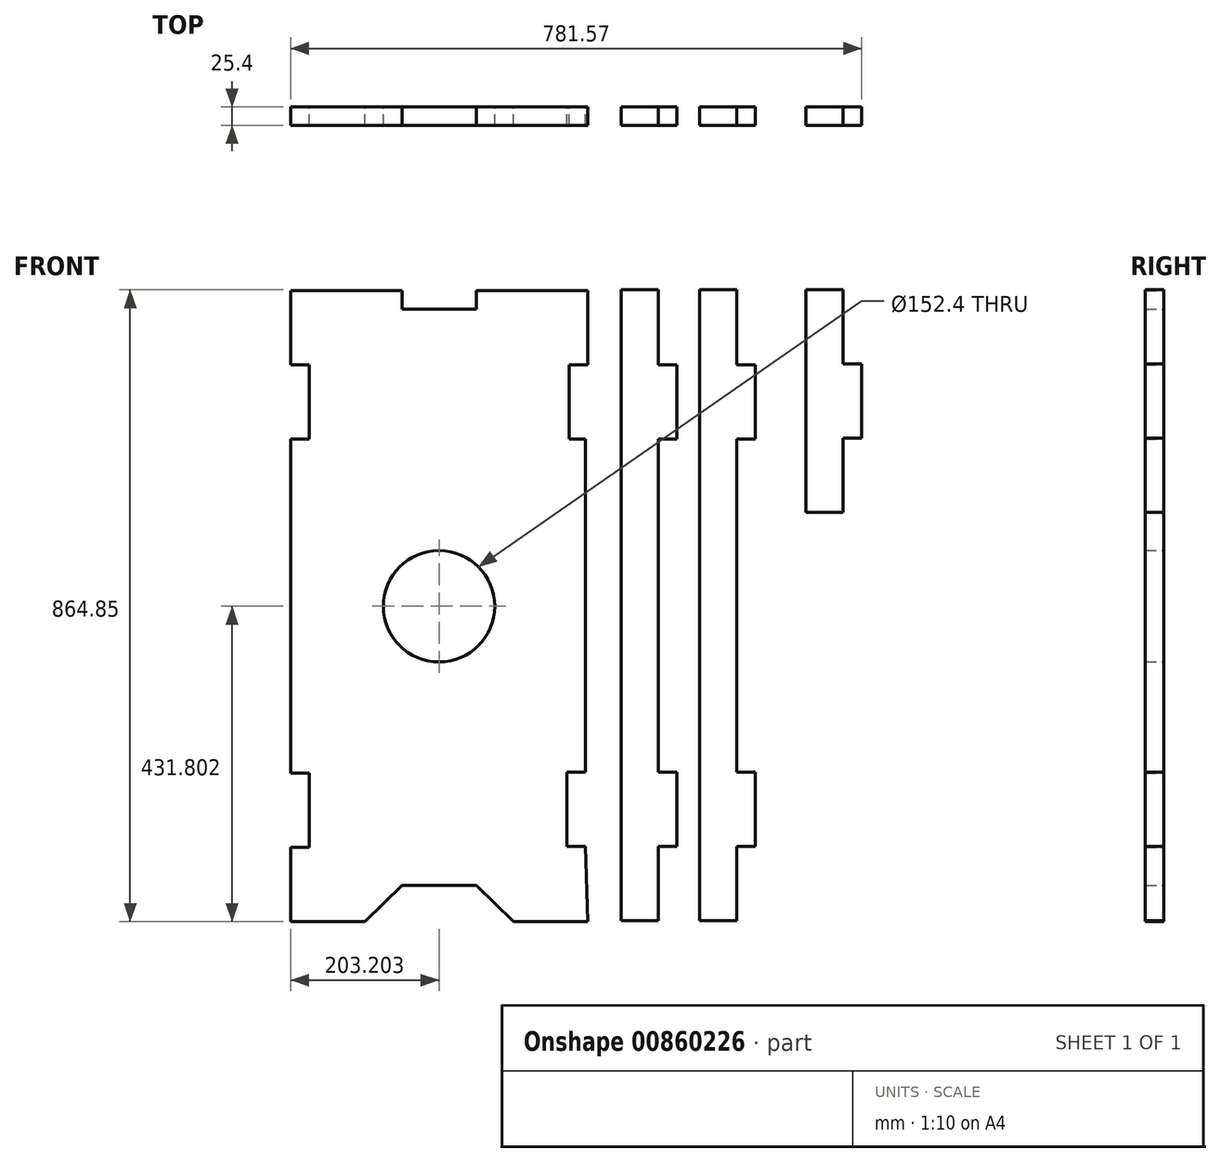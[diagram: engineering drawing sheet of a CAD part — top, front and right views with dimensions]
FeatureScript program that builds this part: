
annotation { "Feature Type Name" : "Feature", "Feature Type Description" : "" }
export const myFeature = defineFeature(function(context is Context, id is Id, definition is map)
    precondition{}
    {
        {
            var Q0;
            Q0=qCreatedBy(makeId("Front.planeOp"),FACE);
            var sketch = newSketch(context, id + "F0", { "sketchPlane" : qUnion([Q0])});
            skLineSegment(sketch, "E0", {"start": v(-277.43, -76.32) * mm, "end": v(-175.83, -76.32) * mm});
            skLineSegment(sketch, "E1", {"start": v(128.97, -76.32) * mm, "end": v(27.37, -76.32) * mm});
            skLineSegment(sketch, "E2", {"start": v(-125.03, -26.44) * mm, "end": v(-23.43, -26.44) * mm});
            skLineSegment(sketch, "E3", {"start": v(-175.83, -76.32) * mm, "end": v(-125.03, -26.44) * mm});
            skLineSegment(sketch, "E4", {"start": v(27.37, -76.32) * mm, "end": v(-23.43, -26.44) * mm});
            skLineSegment(sketch, "E5.bottom", {"start": v(175.18, 788.53) * mm, "end": v(225.98, 788.53) * mm});
            skLineSegment(sketch, "E5.top", {"start": v(175.18, -75.07) * mm, "end": v(225.98, -75.07) * mm});
            skLineSegment(sketch, "E5.left", {"start": v(175.18, 788.53) * mm, "end": v(175.18, -75.07) * mm});
            skLineSegment(sketch, "E6", {"start": v(225.98, 788.53) * mm, "end": v(225.98, 685.68) * mm});
            skLineSegment(sketch, "E7", {"start": v(225.98, 685.68) * mm, "end": v(251.38, 685.68) * mm});
            skLineSegment(sketch, "E8", {"start": v(251.38, 685.68) * mm, "end": v(251.38, 584.08) * mm});
            skLineSegment(sketch, "E9", {"start": v(251.38, 584.08) * mm, "end": v(225.98, 584.08) * mm});
            skLineSegment(sketch, "E10", {"start": v(225.98, -75.07) * mm, "end": v(225.98, 26.53) * mm});
            skLineSegment(sketch, "E11", {"start": v(225.98, 26.53) * mm, "end": v(251.38, 26.53) * mm});
            skLineSegment(sketch, "E12", {"start": v(251.38, 26.53) * mm, "end": v(251.38, 128.13) * mm});
            skLineSegment(sketch, "E13", {"start": v(225.98, 128.13) * mm, "end": v(251.38, 128.13) * mm});
            skLineSegment(sketch, "E14", {"start": v(225.98, 128.13) * mm, "end": v(225.98, 584.08) * mm});
            skLineSegment(sketch, "E15", {"start": v(128.97, 685.68) * mm, "end": v(103.57, 685.68) * mm});
            skLineSegment(sketch, "E16", {"start": v(103.57, 584.08) * mm, "end": v(103.57, 685.68) * mm});
            skLineSegment(sketch, "E17", {"start": v(103.57, 584.08) * mm, "end": v(126.4, 584.08) * mm});
            skLineSegment(sketch, "E18", {"start": v(128.97, 685.68) * mm, "end": v(128.97, 787.28) * mm});
            skLineSegment(sketch, "E19", {"start": v(126.4, 584.08) * mm, "end": v(126.4, 128.13) * mm});
            skLineSegment(sketch, "E20", {"start": v(126.4, 128.13) * mm, "end": v(101, 128.13) * mm});
            skLineSegment(sketch, "E21", {"start": v(101, 128.13) * mm, "end": v(101, 26.53) * mm});
            skLineSegment(sketch, "E22", {"start": v(101, 26.53) * mm, "end": v(126.4, 26.53) * mm});
            skLineSegment(sketch, "E23", {"start": v(126.4, 26.53) * mm, "end": v(128.97, -76.32) * mm});
            skLineSegment(sketch, "E24", {"start": v(-277.43, 685.68) * mm, "end": v(-252.03, 685.68) * mm});
            skLineSegment(sketch, "E25", {"start": v(-252.03, 685.68) * mm, "end": v(-252.03, 584.08) * mm});
            skLineSegment(sketch, "E26", {"start": v(-277.43, 584.08) * mm, "end": v(-252.03, 584.08) * mm});
            skLineSegment(sketch, "E27", {"start": v(-277.43, -76.32) * mm, "end": v(-277.43, 25.28) * mm});
            skLineSegment(sketch, "E28", {"start": v(-277.43, 25.28) * mm, "end": v(-252.03, 25.28) * mm});
            skLineSegment(sketch, "E29", {"start": v(-252.03, 25.28) * mm, "end": v(-252.03, 126.88) * mm});
            skLineSegment(sketch, "E30", {"start": v(-252.03, 126.88) * mm, "end": v(-277.43, 126.88) * mm});
            skLineSegment(sketch, "E31", {"start": v(-277.43, 787.28) * mm, "end": v(-277.43, 685.68) * mm});
            skLineSegment(sketch, "E32", {"start": v(-277.43, 584.08) * mm, "end": v(-277.43, 126.88) * mm});
            skLineSegment(sketch, "E33.bottom", {"start": v(282.37, 788.53) * mm, "end": v(333.17, 788.53) * mm});
            skLineSegment(sketch, "E33.top", {"start": v(282.37, -75.07) * mm, "end": v(333.17, -75.07) * mm});
            skLineSegment(sketch, "E33.left", {"start": v(282.37, 788.53) * mm, "end": v(282.37, -75.07) * mm});
            skLineSegment(sketch, "E34", {"start": v(333.17, 788.53) * mm, "end": v(333.17, 685.68) * mm});
            skLineSegment(sketch, "E35", {"start": v(333.17, 685.68) * mm, "end": v(358.57, 685.68) * mm});
            skLineSegment(sketch, "E36", {"start": v(358.57, 685.68) * mm, "end": v(358.57, 584.08) * mm});
            skLineSegment(sketch, "E37", {"start": v(358.57, 584.08) * mm, "end": v(333.17, 584.08) * mm});
            skLineSegment(sketch, "E38", {"start": v(333.17, -75.07) * mm, "end": v(333.17, 26.53) * mm});
            skLineSegment(sketch, "E39", {"start": v(333.17, 26.53) * mm, "end": v(358.57, 26.53) * mm});
            skLineSegment(sketch, "E40", {"start": v(358.57, 26.53) * mm, "end": v(358.57, 128.13) * mm});
            skLineSegment(sketch, "E41", {"start": v(333.17, 128.13) * mm, "end": v(358.57, 128.13) * mm});
            skLineSegment(sketch, "E42", {"start": v(333.17, 128.13) * mm, "end": v(333.17, 584.08) * mm});
            skLineSegment(sketch, "E43", {"start": v(427.94, 788.53) * mm, "end": v(427.94, 483.73) * mm});
            skLineSegment(sketch, "E44", {"start": v(427.94, 483.73) * mm, "end": v(478.74, 483.73) * mm});
            skLineSegment(sketch, "E45", {"start": v(427.94, 788.53) * mm, "end": v(478.74, 788.53) * mm});
            skLineSegment(sketch, "E46", {"start": v(478.74, 788.53) * mm, "end": v(478.74, 686.93) * mm});
            skLineSegment(sketch, "E47", {"start": v(478.74, 483.73) * mm, "end": v(478.74, 585.33) * mm});
            skLineSegment(sketch, "E48", {"start": v(478.74, 585.33) * mm, "end": v(504.14, 585.33) * mm});
            skLineSegment(sketch, "E49", {"start": v(504.14, 585.33) * mm, "end": v(504.14, 686.93) * mm});
            skLineSegment(sketch, "E50", {"start": v(504.14, 686.93) * mm, "end": v(478.74, 686.93) * mm});
            skLineSegment(sketch, "E51", {"start": v(-125.03, 787.28) * mm, "end": v(-125.03, 761.88) * mm});
            skLineSegment(sketch, "E52", {"start": v(-125.03, 761.88) * mm, "end": v(-23.43, 761.88) * mm});
            skLineSegment(sketch, "E53", {"start": v(-23.43, 787.28) * mm, "end": v(-23.43, 761.88) * mm});
            skLineSegment(sketch, "E54", {"start": v(-277.43, 787.28) * mm, "end": v(-125.03, 787.28) * mm});
            skLineSegment(sketch, "E55", {"start": v(-23.43, 787.28) * mm, "end": v(128.97, 787.28) * mm});
            skCircle(sketch, "E56", {"center": v(-74.23, 355.48) * mm, "radius": 76.2 * mm});
            skPoint(sketch, "E56.centerSnap0", {"position": v(-277.43, 355.48) * mm});
            skPoint(sketch, "E56.centerSnap1", {"position": v(-74.23, 761.88) * mm});
            skSolve(sketch);
        }
        {
            var Q0;
            Q0=makeQuery(id+"F0.imprint","IMPRINT",FACE,{"disambiguationData":[TD([[makeQuery(id+"F0.imprint","IMPRINT",EDGE,{"derivedFrom":sQuery(id+"F0.wireOp",EDGE,"E0")}),1.0]])]});
            var Q1;
            Q1=makeQuery(id+"F0.imprint","IMPRINT",FACE,{"disambiguationData":[TD([[makeQuery(id+"F0.imprint","IMPRINT",EDGE,{"derivedFrom":sQuery(id+"F0.wireOp",EDGE,"E5.bottom")}),-1.0]])]});
            var Q2;
            Q2=makeQuery(id+"F0.imprint","IMPRINT",FACE,{"disambiguationData":[TD([[makeQuery(id+"F0.imprint","IMPRINT",EDGE,{"derivedFrom":sQuery(id+"F0.wireOp",EDGE,"E33.bottom")}),-1.0]])]});
            var Q3;
            Q3=makeQuery(id+"F0.imprint","IMPRINT",FACE,{"disambiguationData":[TD([[makeQuery(id+"F0.imprint","IMPRINT",EDGE,{"derivedFrom":sQuery(id+"F0.wireOp",EDGE,"E43")}),1.0]])]});
            extrude(context, id + "F1", {"entities" : qUnion([Q0, Q1, Q2, Q3]), "depth" : 25.4 * mm, "offsetDistance" : 25.4 * mm});
        }
    });
